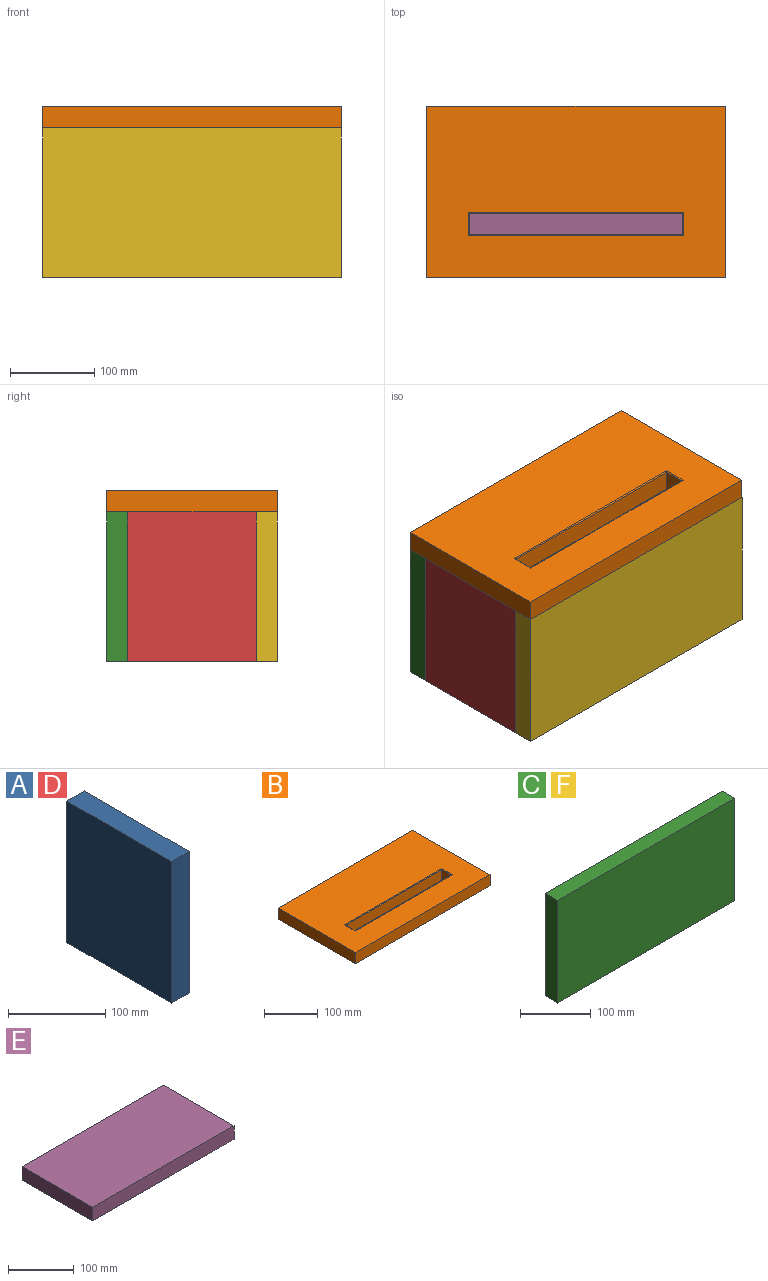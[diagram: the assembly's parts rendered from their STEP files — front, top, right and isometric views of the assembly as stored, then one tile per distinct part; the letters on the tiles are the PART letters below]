
ASSEMBLY  parts=6 mates=5
PART A: 6 faces, bbox 25.4x152.4x177.8 mm
  f0: plane 152.4x25.4mm, normal (0,0,-1), area 3871mm2, adj f1,f3,f4,f5
  f1: plane 177.8x25.4mm, normal (0,1,0), area 4516.1mm2, adj f0,f2,f4,f5
  f2: plane 152.4x25.4mm, normal (0,0,1), area 3871mm2, adj f1,f3,f4,f5
  f3: plane 177.8x25.4mm, normal (0,-1,0), area 4516.1mm2, adj f0,f2,f4,f5
  f4: plane 177.8x152.4mm, normal (1,0,0), area 27096.7mm2, adj f0,f1,f2,f3
  f5: plane 177.8x152.4mm, normal (-1,0,0), area 27096.7mm2, adj f0,f1,f2,f3
PART B: 14 faces, bbox 355.6x203.2x25.4 mm
  f0: plane 355.6x25.4mm, normal (0,-1,0), area 9032.2mm2, adj f1,f3,f4,f5
  f1: plane 203.2x25.4mm, normal (1,0,0), area 5161.3mm2, adj f0,f2,f4,f5
  f2: plane 355.6x25.4mm, normal (0,1,0), area 9032.2mm2, adj f1,f3,f4,f5
  f3: plane 203.2x25.4mm, normal (-1,0,0), area 5161.3mm2, adj f0,f2,f4,f5
  f4: plane 355.6x203.2mm, normal (0,0,1), area 65090.2mm2, adj f0,f1,f2,f3,f10,f11,f12,f13
  f5: plane 355.6x203.2mm, normal (0,0,-1), area 65806.3mm2, adj f0,f1,f2,f3,f6,f7,f8,f9
  f6: plane 254x24.13mm, normal (0,1,0), area 6129mm2, adj f5,f7,f8,f11
  f7: plane 25.4x24.13mm, normal (1,0,0), area 612.9mm2, adj f5,f6,f9,f10
  f8: plane 25.4x24.13mm, normal (-1,0,0), area 612.9mm2, adj f5,f6,f9,f13
  f9: plane 254x24.13mm, normal (0,-1,0), area 6129mm2, adj f5,f7,f8,f12
  f10: cylinder r=1.27mm len=27.94mm, axis (0,1,0), area 52.5mm2, adj f4,f7,f11,f12
  f11: cylinder r=1.27mm len=256.54mm, axis (-1,0,0), area 508.5mm2, adj f4,f6,f10,f13
  f12: cylinder r=1.27mm len=256.54mm, axis (1,0,0), area 508.5mm2, adj f4,f9,f10,f13
  f13: cylinder r=1.27mm len=27.94mm, axis (0,-1,0), area 52.5mm2, adj f4,f8,f11,f12
PART C: 6 faces, bbox 355.6x25.4x177.8 mm
  f0: plane 355.6x25.4mm, normal (0,0,-1), area 9032.2mm2, adj f1,f3,f4,f5
  f1: plane 177.8x25.4mm, normal (1,0,0), area 4516.1mm2, adj f0,f2,f4,f5
  f2: plane 355.6x25.4mm, normal (0,0,1), area 9032.2mm2, adj f1,f3,f4,f5
  f3: plane 177.8x25.4mm, normal (-1,0,0), area 4516.1mm2, adj f0,f2,f4,f5
  f4: plane 355.6x177.8mm, normal (0,-1,0), area 63225.7mm2, adj f0,f1,f2,f3
  f5: plane 355.6x177.8mm, normal (0,1,0), area 63225.7mm2, adj f0,f1,f2,f3
PART D: same geometry as A
PART E: 6 faces, bbox 304.8x152.4x25.4 mm
  f0: plane 304.8x25.4mm, normal (0,-1,0), area 7741.9mm2, adj f1,f3,f4,f5
  f1: plane 152.4x25.4mm, normal (1,0,0), area 3871mm2, adj f0,f2,f4,f5
  f2: plane 304.8x25.4mm, normal (0,1,0), area 7741.9mm2, adj f1,f3,f4,f5
  f3: plane 152.4x25.4mm, normal (-1,0,0), area 3871mm2, adj f0,f2,f4,f5
  f4: plane 304.8x152.4mm, normal (0,0,1), area 46451.5mm2, adj f0,f1,f2,f3
  f5: plane 304.8x152.4mm, normal (0,0,-1), area 46451.5mm2, adj f0,f1,f2,f3
PART F: same geometry as C
PLACE A t=(152.4,-101.6,0)mm
PLACE B t=(0,-101.6,88.9)mm
PLACE C at identity fixed
PLACE D t=(-177.8,-101.6,0)mm
PLACE E t=(0,-101.6,-88.9)mm
PLACE F t=(0,-177.8,0)mm
MATE fastened B.f5 <-> F.f2  axis (0,0,-1) through (0,-203.2,88.9)mm
MATE fastened D.f4 <-> E.f3  axis (1,0,0) through (-152.4,-101.6,-88.9)mm
MATE fastened A.f5 <-> E.f1  axis (-1,0,0) through (152.4,-101.6,-88.9)mm
MATE fastened E.f2 <-> C.f4  axis (0,1,0) through (0,-25.4,-88.9)mm
MATE fastened F.f5 <-> E.f0  axis (0,1,0) through (0,-177.8,-88.9)mm
